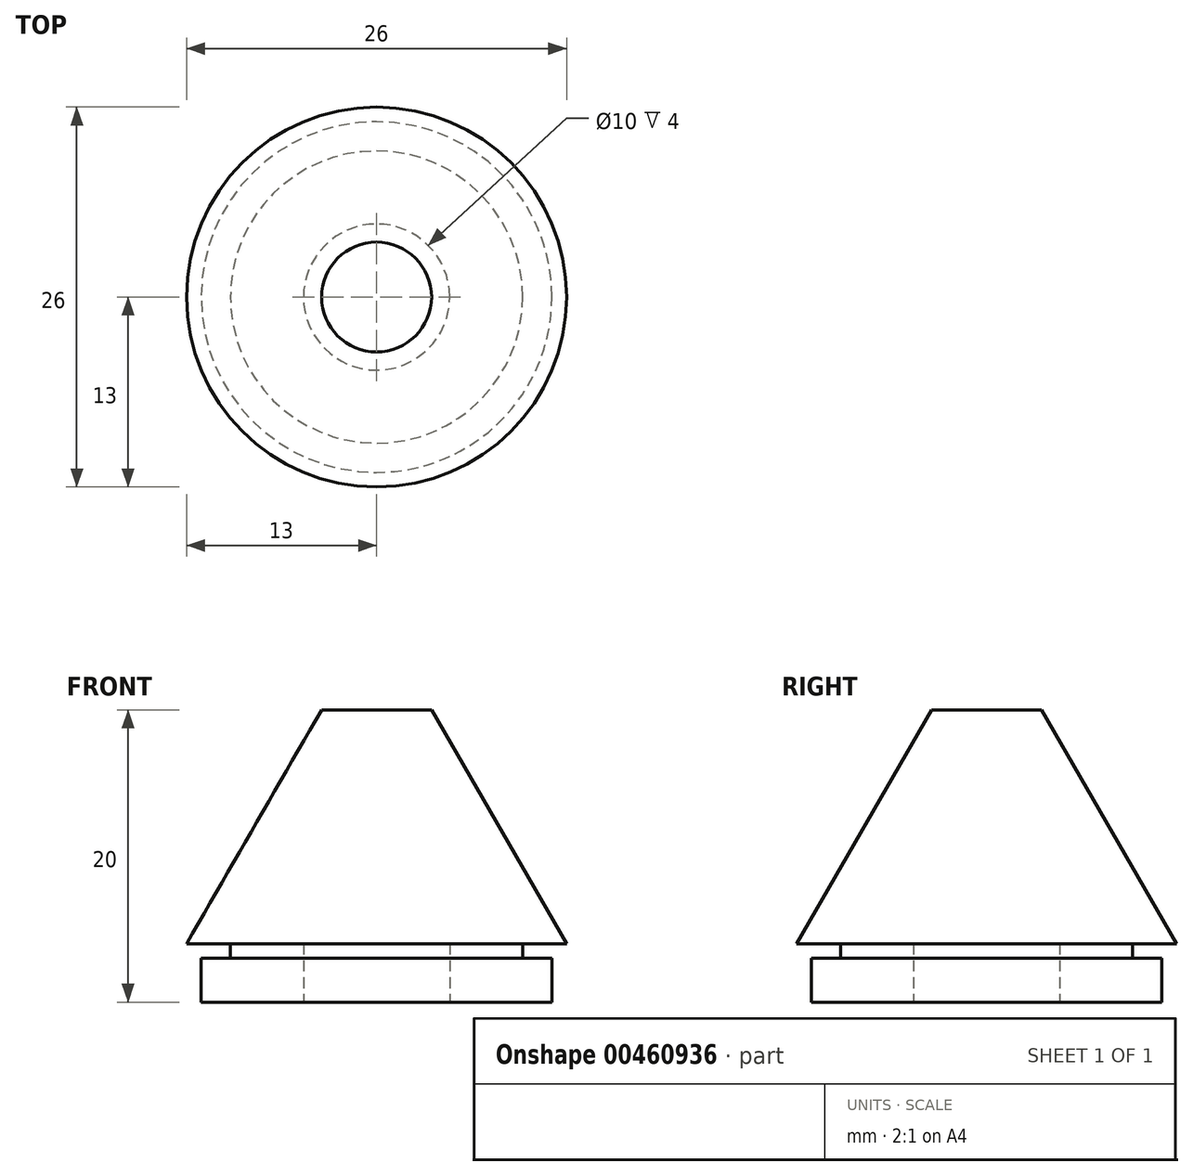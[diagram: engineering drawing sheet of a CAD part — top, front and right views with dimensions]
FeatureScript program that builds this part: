
annotation { "Feature Type Name" : "Feature", "Feature Type Description" : "" }
export const myFeature = defineFeature(function(context is Context, id is Id, definition is map)
    precondition{}
    {
        {
            var Q0;
            Q0=qCreatedBy(makeId("Right.planeOp"),FACE);
            var sketch = newSketch(context, id + "F0", { "sketchPlane" : qUnion([Q0])});
            skLineSegment(sketch, "E0", {"start": v(0, -10.16) * mm, "end": v(0, 20) * mm, "construction": true});
            skLineSegment(sketch, "E1", {"start": v(-5, 0) * mm, "end": v(-12, 0) * mm});
            skLineSegment(sketch, "E2", {"start": v(-12, 0) * mm, "end": v(-12, 3) * mm});
            skLineSegment(sketch, "E3", {"start": v(-12, 3) * mm, "end": v(-10, 3) * mm});
            skLineSegment(sketch, "E4", {"start": v(-10, 3) * mm, "end": v(-10, 4) * mm});
            skLineSegment(sketch, "E5", {"start": v(-10, 4) * mm, "end": v(-13, 4) * mm});
            skLineSegment(sketch, "E6", {"start": v(-13, 4) * mm, "end": v(-3.76, 20) * mm});
            skLineSegment(sketch, "E7", {"start": v(-3.76, 20) * mm, "end": v(0, 20) * mm});
            skLineSegment(sketch, "E8", {"start": v(-5, 0) * mm, "end": v(-5, 4) * mm});
            skLineSegment(sketch, "E9", {"start": v(-5, 4) * mm, "end": v(0, 4) * mm});
            skLineSegment(sketch, "E10", {"start": v(-5, 0) * mm, "end": v(0, 0) * mm, "construction": true});
            skLineSegment(sketch, "E11", {"start": v(-10, 4) * mm, "end": v(-5, 4) * mm, "construction": true});
            skLineSegment(sketch, "E12", {"start": v(0, 20) * mm, "end": v(0, 4) * mm});
            skSolve(sketch);
        }
        {
            var Q0;
            Q0 = qSketchRegion(id + "F0", true);
            var Q1;
            Q1=sQuery(id+"F0.wireOp",EDGE,"E0");
            revolve(context, id + "F1", {"surfaceOperationType" : NewSurfaceOperationType.NEW, "entities" : qUnion([Q0]), "axis" : qUnion([Q1]), "revolveType" : RevolveType.FULL});
        }
    });
